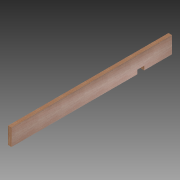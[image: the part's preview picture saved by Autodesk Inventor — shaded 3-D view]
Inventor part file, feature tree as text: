
AUTODESK INVENTOR PART (.ipt)
format: ipt  version: 2015 (Build 190159000, 159)  size: 91,648 bytes
history: native  units: in
note: dims shown in document units (in); Inventor stores cm internally (conversion verified against a paired STEP export)
features: extrude x2, sketch x2
ambient origin geometry x8: Origin, YZ Plane, XZ Plane, XY Plane, X Axis, Y Axis, Z Axis, Center Point
bodies: Solid1 (feature_tree)
feature tree (4):
  extrude  "Extrusion1"  Depth=7.25in
  extrude  "Extrusion2"  Depth=1.75in
  sketch  "Sketch1"  dims[d0=1.5in d1=7.25in]
  sketch  "Sketch2"  dims[d2=69.48in d3=0.0in d4=1.75in d5=3.0in d6=12.0in d7=1.0in d8=0.0in]
